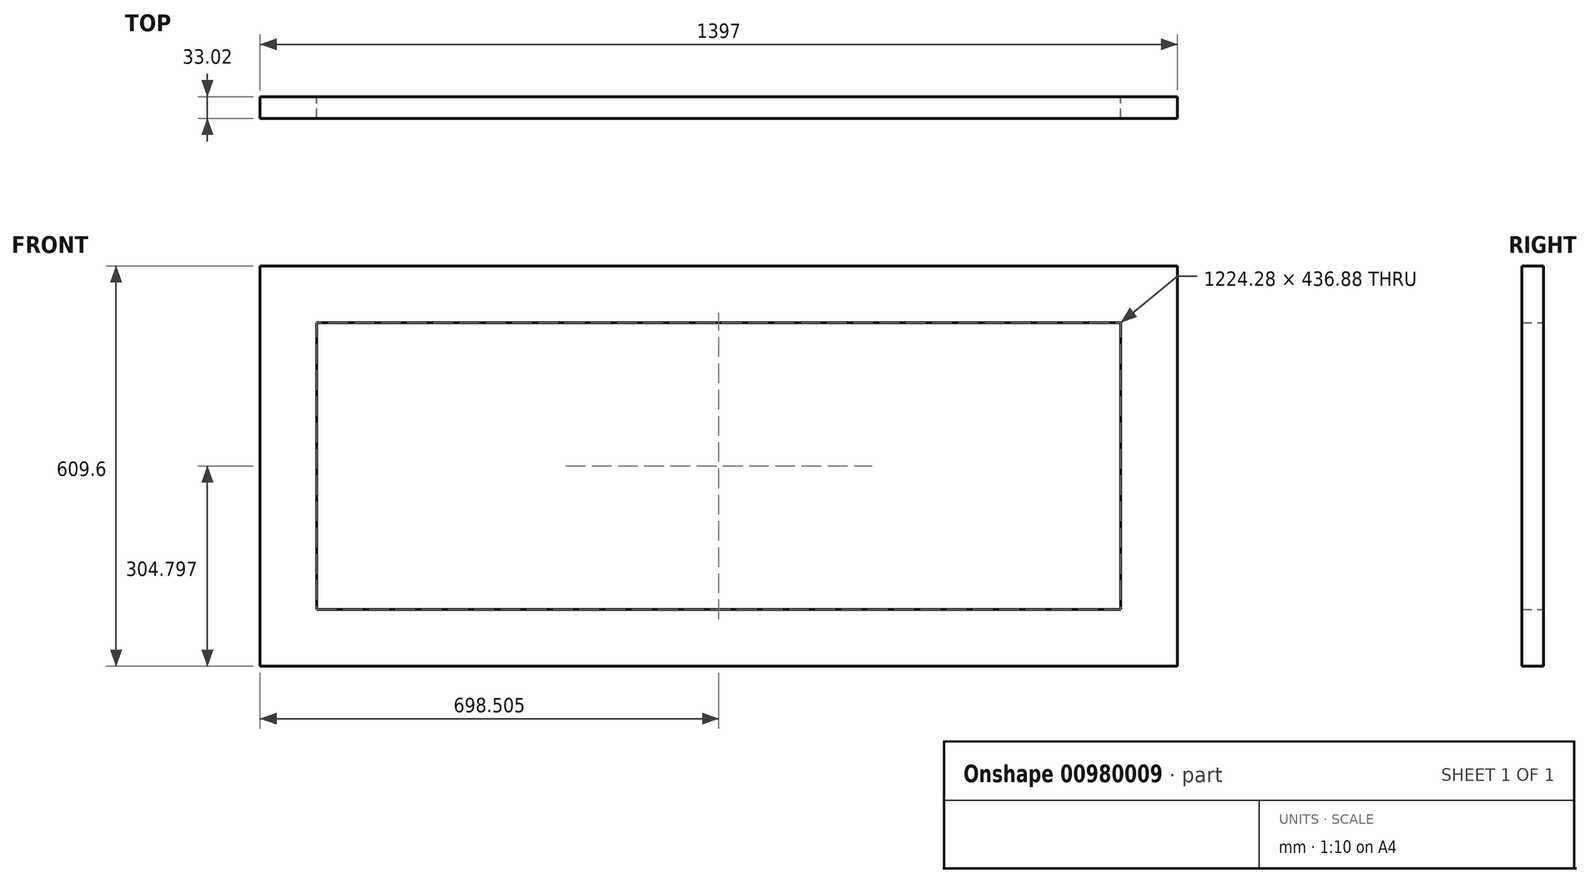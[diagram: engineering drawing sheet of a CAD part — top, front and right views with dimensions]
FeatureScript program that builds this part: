
annotation { "Feature Type Name" : "Feature", "Feature Type Description" : "" }
export const myFeature = defineFeature(function(context is Context, id is Id, definition is map)
    precondition{}
    {
        {
            var Q0;
            Q0=qCreatedBy(makeId("Front.planeOp"),FACE);
            var sketch = newSketch(context, id + "F0", { "sketchPlane" : qUnion([Q0])});
            skLineSegment(sketch, "E0.bottom", {"start": v(-751.18, 189) * mm, "end": v(645.82, 189) * mm});
            skLineSegment(sketch, "E0.top", {"start": v(-751.18, -420.6) * mm, "end": v(645.82, -420.6) * mm});
            skLineSegment(sketch, "E0.left", {"start": v(-751.18, 189) * mm, "end": v(-751.18, -420.6) * mm});
            skLineSegment(sketch, "E0.right", {"start": v(645.82, 189) * mm, "end": v(645.82, -420.6) * mm});
            skLineSegment(sketch, "E1.0", {"start": v(-664.82, 102.64) * mm, "end": v(559.46, 102.64) * mm});
            skLineSegment(sketch, "E1.1", {"start": v(-664.82, 102.64) * mm, "end": v(-664.82, -334.24) * mm});
            skLineSegment(sketch, "E1.2", {"start": v(-664.82, -334.24) * mm, "end": v(559.46, -334.24) * mm});
            skLineSegment(sketch, "E1.3", {"start": v(559.46, 102.64) * mm, "end": v(559.46, -334.24) * mm});
            skSolve(sketch);
        }
        {
            var Q0;
            Q0=makeQuery(id+"F0.imprint","IMPRINT",FACE,{"disambiguationData":[TD([[makeQuery(id+"F0.imprint","IMPRINT",EDGE,{"derivedFrom":sQuery(id+"F0.wireOp",EDGE,"E0.bottom")}),-1.0]])]});
            extrude(context, id + "F1", {"entities" : qUnion([Q0]), "depth" : 33.02 * mm, "offsetDistance" : 25.4 * mm});
        }
    });
